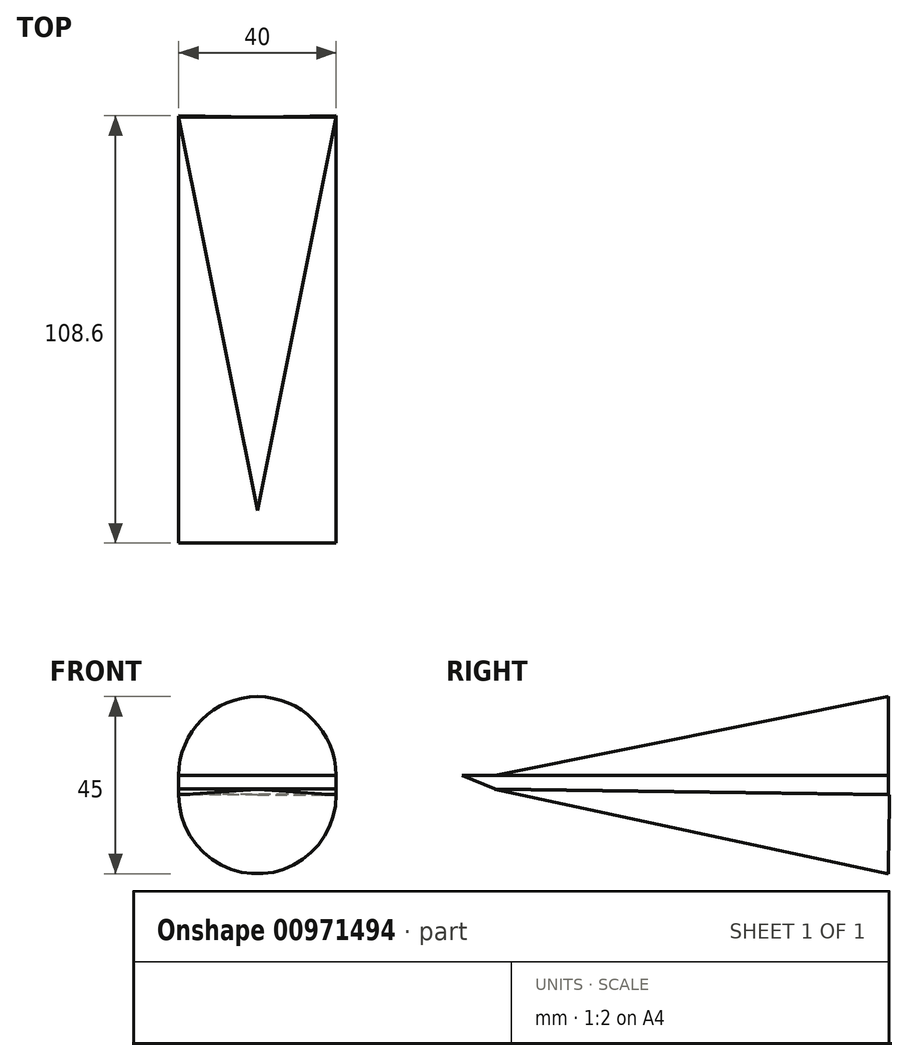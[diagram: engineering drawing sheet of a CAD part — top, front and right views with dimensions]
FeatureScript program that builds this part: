
annotation { "Feature Type Name" : "Feature", "Feature Type Description" : "" }
export const myFeature = defineFeature(function(context is Context, id is Id, definition is map)
    precondition{}
    {
        {
            var Q0;
            Q0=qCreatedBy(makeId("Right.planeOp"),FACE);
            var sketch = newSketch(context, id + "F0", { "sketchPlane" : qUnion([Q0])});
            skLineSegment(sketch, "E0", {"start": v(0, 0) * mm, "end": v(-100, 0) * mm});
            skLineSegment(sketch, "E1", {"start": v(-100, 0) * mm, "end": v(0, 20) * mm});
            skLineSegment(sketch, "E2", {"start": v(0, 0) * mm, "end": v(0, 20) * mm});
            skSolve(sketch);
        }
        {
            var Q0;
            Q0 = qSketchRegion(id + "F0", true);
            var Q1;
            Q1=sQuery(id+"F0.wireOp",EDGE,"E0");
            revolve(context, id + "F1", {"surfaceOperationType" : NewSurfaceOperationType.NEW, "entities" : qUnion([Q0]), "axis" : qUnion([Q1]), "revolveType" : RevolveType.SYMMETRIC, "angle" : 180 * degree});
        }
        {
            var Q0;
            Q0=qCreatedBy(makeId("Right.planeOp"),FACE);
            var sketch = newSketch(context, id + "F2", { "sketchPlane" : qUnion([Q0])});
            skLineSegment(sketch, "E3", {"start": v(0, 0) * mm, "end": v(0, -5) * mm});
            skLineSegment(sketch, "E4", {"start": v(0, -5) * mm, "end": v(0, -25) * mm});
            skLineSegment(sketch, "E5", {"start": v(0, -25) * mm, "end": v(-99.99, -3.51) * mm});
            skLineSegment(sketch, "E6", {"start": v(-99.99, -3.51) * mm, "end": v(0, -5) * mm});
            skSolve(sketch);
        }
        {
            var Q0;
            Q0 = qSketchRegion(id + "F2", true);
            var Q1;
            Q1=sQuery(id+"F2.wireOp",EDGE,"E6");
            revolve(context, id + "F3", {"surfaceOperationType" : NewSurfaceOperationType.NEW, "entities" : qUnion([Q0]), "axis" : qUnion([Q1]), "revolveType" : RevolveType.SYMMETRIC, "angle" : 180 * degree});
        }
        {
            var Q0;
            Q0=qCreatedBy(makeId("Right.planeOp"),FACE);
            var sketch = newSketch(context, id + "F4", { "sketchPlane" : qUnion([Q0])});
            skLineSegment(sketch, "E7", {"start": v(0, 0) * mm, "end": v(-99.99, 0) * mm});
            skLineSegment(sketch, "E8", {"start": v(-99.99, 0) * mm, "end": v(-108.3, 0) * mm});
            skLineSegment(sketch, "E9", {"start": v(-108.3, 0) * mm, "end": v(-99.99, -3.42) * mm});
            skLineSegment(sketch, "E10", {"start": v(-99.99, -3.42) * mm, "end": v(0, -4.79) * mm});
            skLineSegment(sketch, "E11", {"start": v(0, -4.79) * mm, "end": v(0, 0) * mm});
            skSolve(sketch);
        }
        {
            var Q0;
            Q0 = qSketchRegion(id + "F4", true);
            extrude(context, id + "F5", {"entities" : qUnion([Q0]), "operationType" : NewBodyOperationType.ADD, "depth" : 20 * mm, "offsetDistance" : 25 * mm});
        }
        {
            var Q0;
            Q0 = qSketchRegion(id + "F4", true);
            extrude(context, id + "F6", {"entities" : qUnion([Q0]), "operationType" : NewBodyOperationType.ADD, "depth" : -20 * mm, "offsetDistance" : 25 * mm});
        }
    });
